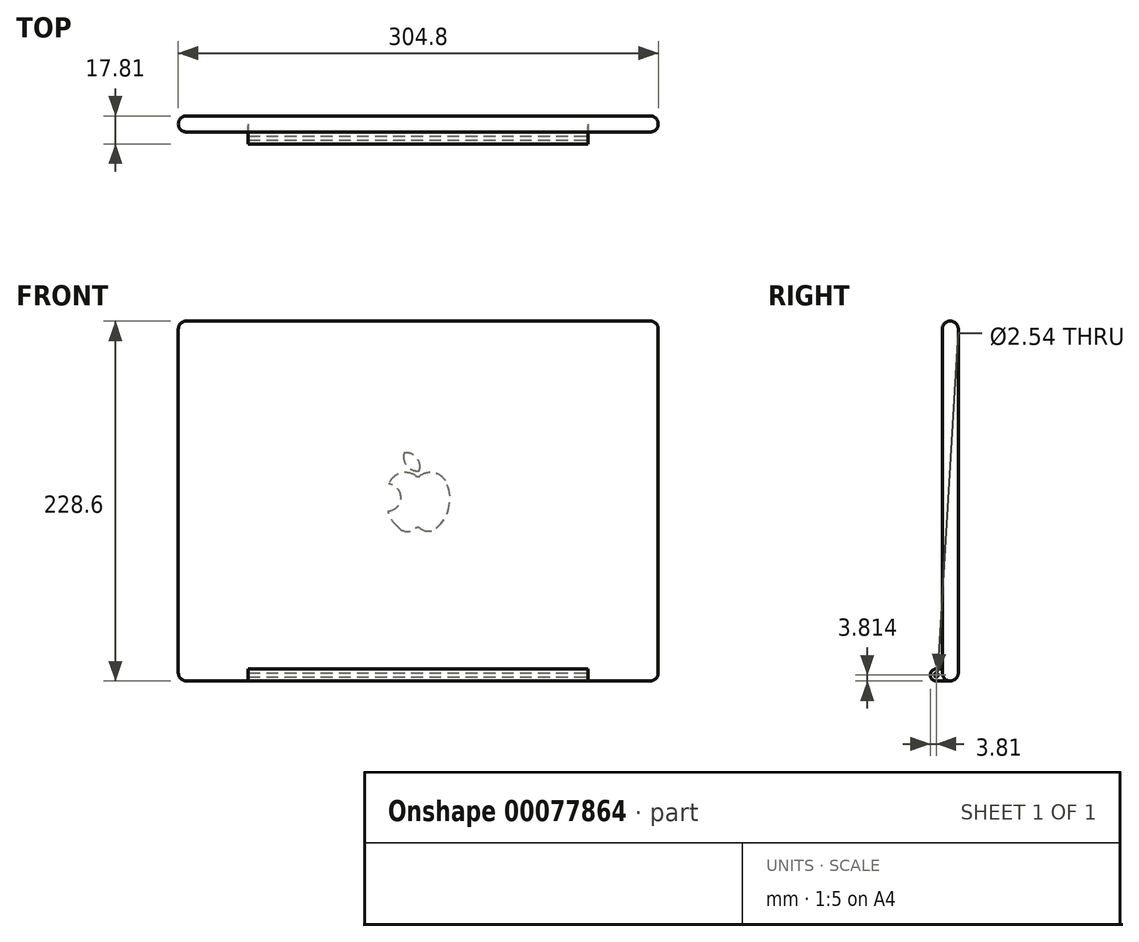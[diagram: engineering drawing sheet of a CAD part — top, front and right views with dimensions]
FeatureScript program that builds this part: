
annotation { "Feature Type Name" : "Feature", "Feature Type Description" : "" }
export const myFeature = defineFeature(function(context is Context, id is Id, definition is map)
    precondition{}
    {
        {
            var Q0;
            Q0=qCreatedBy(makeId("Front.planeOp"),FACE);
            var sketch = newSketch(context, id + "F0", { "sketchPlane" : qUnion([Q0])});
            skLineSegment(sketch, "E0.bottom", {"start": v(-207.35, 122.82) * mm, "end": v(97.45, 122.82) * mm});
            skLineSegment(sketch, "E0.top", {"start": v(-207.35, -105.78) * mm, "end": v(97.45, -105.78) * mm});
            skLineSegment(sketch, "E0.left", {"start": v(-207.35, 122.82) * mm, "end": v(-207.35, -105.78) * mm});
            skLineSegment(sketch, "E0.right", {"start": v(97.45, 122.82) * mm, "end": v(97.45, -105.78) * mm});
            skCircle(sketch, "E1", {"center": v(-54.95, 112.66) * mm, "radius": 3.18 * mm});
            skSolve(sketch);
        }
        {
            var Q0;
            Q0=makeQuery(id+"F0.imprint","IMPRINT",FACE,{"disambiguationData":[TD([[makeQuery(id+"F0.imprint","IMPRINT",EDGE,{"derivedFrom":sQuery(id+"F0.wireOp",EDGE,"E0.bottom")}),-1.0]])]});
            var Q1;
            Q1=makeQuery(id+"F0.imprint","IMPRINT",FACE,{"disambiguationData":[TD([[makeQuery(id+"F0.imprint","IMPRINT",EDGE,{"derivedFrom":sQuery(id+"F0.wireOp",EDGE,"E1")}),1.0]])]});
            extrude(context, id + "F1", {"entities" : qUnion([Q0, Q1]), "depth" : 7.62 * mm});
        }
        {
            var Q0;
            Q0=makeQuery(id+"F1.opExtrude","CAP_EDGE",EDGE,{"disambiguationData":[OSD([sQuery(id+"F0.wireOp",EDGE,"E0.bottom")])],"isStart":true});
            var Q1;
            Q1=makeQuery(id+"F1.opExtrude","CAP_EDGE",EDGE,{"disambiguationData":[OSD([sQuery(id+"F0.wireOp",EDGE,"E0.left")])],"isStart":true});
            var Q2;
            Q2=makeQuery(id+"F1.opExtrude","CAP_EDGE",EDGE,{"disambiguationData":[OSD([sQuery(id+"F0.wireOp",EDGE,"E0.right")])],"isStart":true});
            var Q3;
            Q3=makeQuery(id+"F1.opExtrude","CAP_EDGE",EDGE,{"disambiguationData":[OSD([sQuery(id+"F0.wireOp",EDGE,"E0.top")])],"isStart":true});
            var Q4;
            Q4=makeQuery(id+"F1.opExtrude","SWEPT_EDGE",EDGE,{"disambiguationData":[OSD([sQuery(id+"F0.wireOp",EDGE,"E0.bottom"),sQuery(id+"F0.wireOp",EDGE,"E0.right")])]});
            var Q5;
            Q5=makeQuery(id+"F1.opExtrude","SWEPT_EDGE",EDGE,{"disambiguationData":[OSD([sQuery(id+"F0.wireOp",EDGE,"E0.top"),sQuery(id+"F0.wireOp",EDGE,"E0.right")])]});
            var Q6;
            Q6=makeQuery(id+"F1.opExtrude","SWEPT_EDGE",EDGE,{"disambiguationData":[OSD([sQuery(id+"F0.wireOp",EDGE,"E0.bottom"),sQuery(id+"F0.wireOp",EDGE,"E0.left")])]});
            var Q7;
            Q7=makeQuery(id+"F1.opExtrude","SWEPT_EDGE",EDGE,{"disambiguationData":[OSD([sQuery(id+"F0.wireOp",EDGE,"E0.top"),sQuery(id+"F0.wireOp",EDGE,"E0.left")])]});
            fillet(context, id + "F2", {"entities" : qUnion([Q0, Q1, Q2, Q3, Q4, Q5, Q6, Q7]), "radius" : 5.08 * mm, "tangentPropagation" : true, "allowEdgeOverflow" : false});
        }
        {
            var Q0;
            Q0=makeQuery(id+"F1.opExtrude","CAP_FACE",FACE,{"disambiguationData":[OSD([sQuery(id+"F0.wireOp",EDGE,"E0.bottom"),sQuery(id+"F0.wireOp",EDGE,"E0.top"),sQuery(id+"F0.wireOp",EDGE,"E0.left"),sQuery(id+"F0.wireOp",EDGE,"E0.right")])],"isStart":false});
            var sketch = newSketch(context, id + "F3", { "sketchPlane" : qUnion([Q0])});
            skLineSegment(sketch, "E2.bottom", {"start": v(-188.3, 103.77) * mm, "end": v(78.4, 103.77) * mm});
            skLineSegment(sketch, "E2.top", {"start": v(-188.3, -80.38) * mm, "end": v(78.4, -80.38) * mm});
            skLineSegment(sketch, "E2.left", {"start": v(-188.3, 103.77) * mm, "end": v(-188.3, -80.38) * mm});
            skLineSegment(sketch, "E2.right", {"start": v(78.4, 103.77) * mm, "end": v(78.4, -80.38) * mm});
            skSolve(sketch);
        }
        {
            var Q0;
            Q0=makeQuery(id+"F3.imprint","IMPRINT",FACE,{"disambiguationData":[TD([[makeQuery(id+"F3.imprint","IMPRINT",EDGE,{"derivedFrom":sQuery(id+"F3.wireOp",EDGE,"E2.bottom")}),-1.0]])]});
            extrude(context, id + "F4", {"entities" : qUnion([Q0]), "operationType" : NewBodyOperationType.ADD, "depth" : 2.54 * mm});
        }
        {
            var Q0;
            Q0=makeQuery(id+"F3.imprint","IMPRINT",FACE,{"disambiguationData":[TD([[makeQuery(id+"F3.imprint","IMPRINT",EDGE,{"derivedFrom":sQuery(id+"F3.wireOp",EDGE,"E2.bottom")}),1.0]])]});
            extrude(context, id + "F5", {"entities" : qUnion([Q0]), "depth" : 2.54 * mm});
        }
        {
            var Q0;
            Q0=makeQuery(id+"F5.opExtrude","CAP_FACE",FACE,{"disambiguationData":[OSD([sQuery(id+"F0.wireOp",EDGE,"E0.bottom"),sQuery(id+"F0.wireOp",EDGE,"E0.top"),sQuery(id+"F0.wireOp",EDGE,"E0.left"),sQuery(id+"F0.wireOp",EDGE,"E0.right"),sQuery(id+"F3.wireOp",EDGE,"E2.bottom"),sQuery(id+"F3.wireOp",EDGE,"E2.top"),sQuery(id+"F3.wireOp",EDGE,"E2.left"),sQuery(id+"F3.wireOp",EDGE,"E2.right")])],"isStart":false});
            var sketch = newSketch(context, id + "F6", { "sketchPlane" : qUnion([Q0])});
            skLineSegment(sketch, "E3.bottom", {"start": v(-162.9, -105.78) * mm, "end": v(53, -105.78) * mm});
            skLineSegment(sketch, "E3.top", {"start": v(-162.9, -98.16) * mm, "end": v(53, -98.16) * mm});
            skLineSegment(sketch, "E3.left", {"start": v(-162.9, -105.78) * mm, "end": v(-162.9, -98.16) * mm});
            skLineSegment(sketch, "E3.right", {"start": v(53, -105.78) * mm, "end": v(53, -98.16) * mm});
            skSolve(sketch);
        }
        {
            var Q0;
            Q0=makeQuery(id+"F6.imprint","IMPRINT",FACE,{"disambiguationData":[TD([[makeQuery(id+"F6.imprint","IMPRINT",EDGE,{"derivedFrom":sQuery(id+"F6.wireOp",EDGE,"E3.bottom")}),1.0]])]});
            extrude(context, id + "F7", {"entities" : qUnion([Q0]), "operationType" : NewBodyOperationType.ADD, "depth" : 7.62 * mm});
        }
        {
            var Q0;
            Q0=makeQuery(id+"F7.opExtrude","SWEPT_FACE",FACE,{"disambiguationData":[OSD([sQuery(id+"F6.wireOp",EDGE,"E3.right")])]});
            var sketch = newSketch(context, id + "F8", { "sketchPlane" : qUnion([Q0])});
            skCircle(sketch, "E4", {"center": v(-13.97, -101.97) * mm, "radius": 1.27 * mm});
            skSolve(sketch);
        }
        {
            var Q0;
            Q0=makeQuery(id+"F7.opExtrude","CAP_EDGE",EDGE,{"disambiguationData":[OSD([sQuery(id+"F6.wireOp",EDGE,"E3.top")])],"isStart":false});
            var Q1;
            Q1=makeQuery(id+"F7.opExtrude","CAP_EDGE",EDGE,{"disambiguationData":[OSD([sQuery(id+"F6.wireOp",EDGE,"E3.bottom")])],"isStart":false});
            fillet(context, id + "F9", {"entities" : qUnion([Q0, Q1]), "radius" : 3.8 * mm, "tangentPropagation" : true, "allowEdgeOverflow" : false});
        }
        {
            var Q0;
            Q0=makeQuery(id+"F8.imprint","IMPRINT",FACE,{"disambiguationData":[TD([[makeQuery(id+"F8.imprint","IMPRINT",EDGE,{"derivedFrom":sQuery(id+"F8.wireOp",EDGE,"E4")}),1.0]])]});
            extrude(context, id + "F10", {"entities" : qUnion([Q0]), "operationType" : NewBodyOperationType.REMOVE, "oppositeDirection" : true, "depth" : 215.9 * mm});
        }
        {
            var Q0;
            Q0=makeQuery(id+"F0.imprint","IMPRINT",FACE,{"disambiguationData":[TD([[makeQuery(id+"F0.imprint","IMPRINT",EDGE,{"derivedFrom":sQuery(id+"F0.wireOp",EDGE,"E1")}),1.0]])]});
            extrude(context, id + "F11", {"entities" : qUnion([Q0]), "operationType" : NewBodyOperationType.ADD, "depth" : 10.16 * mm});
        }
        {
            var Q0;
            Q0=makeQuery(id+"F5.opExtrude","CAP_EDGE",EDGE,{"disambiguationData":[OSD([sQuery(id+"F0.wireOp",EDGE,"E0.left")])],"isStart":false});
            var Q1;
            {var subQ0=sQuery(id+"F0.wireOp",EDGE,"E0.bottom");var subQ1=sQuery(id+"F0.wireOp",EDGE,"E0.top");var subQ2=sQuery(id+"F0.wireOp",EDGE,"E0.left");var subQ3=sQuery(id+"F0.wireOp",EDGE,"E0.right");Q1=makeQuery(id+"F5.opExtrude","CAP_EDGE",EDGE,{"disambiguationData":[OSD([subQ0,subQ1,subQ2,subQ3]),TDD([makeQuery(id+"F3.imprint","IMPRINT",EDGE,{"derivedFrom":makeQuery(id+"F2.opFillet","BLEND_EDGE",EDGE,{"blendedFrom":[makeQuery(id+"F1.opExtrude","SWEPT_EDGE",EDGE,{"disambiguationData":[OSD([subQ0,subQ2])]}),makeQuery(id+"F1.opExtrude","CAP_FACE",FACE,{"disambiguationData":[OSD([subQ0,subQ1,subQ2,subQ3])],"isStart":false})],"blendedInto":[makeQuery(id+"F1.opExtrude","CAP_FACE",FACE,{"disambiguationData":[OSD([subQ0,subQ1,subQ2,subQ3])],"isStart":false})]})})])],"isStart":false});}
            var Q2;
            Q2=makeQuery(id+"F5.opExtrude","CAP_EDGE",EDGE,{"disambiguationData":[OSD([sQuery(id+"F0.wireOp",EDGE,"E0.bottom")])],"isStart":false});
            var Q3;
            {var subQ0=sQuery(id+"F0.wireOp",EDGE,"E0.bottom");var subQ1=sQuery(id+"F0.wireOp",EDGE,"E0.top");var subQ2=sQuery(id+"F0.wireOp",EDGE,"E0.left");var subQ3=sQuery(id+"F0.wireOp",EDGE,"E0.right");Q3=makeQuery(id+"F5.opExtrude","CAP_EDGE",EDGE,{"disambiguationData":[OSD([subQ0,subQ1,subQ2,subQ3]),TDD([makeQuery(id+"F3.imprint","IMPRINT",EDGE,{"derivedFrom":makeQuery(id+"F2.opFillet","BLEND_EDGE",EDGE,{"blendedFrom":[makeQuery(id+"F1.opExtrude","SWEPT_EDGE",EDGE,{"disambiguationData":[OSD([subQ0,subQ3])]}),makeQuery(id+"F1.opExtrude","CAP_FACE",FACE,{"disambiguationData":[OSD([subQ0,subQ1,subQ2,subQ3])],"isStart":false})],"blendedInto":[makeQuery(id+"F1.opExtrude","CAP_FACE",FACE,{"disambiguationData":[OSD([subQ0,subQ1,subQ2,subQ3])],"isStart":false})]})})])],"isStart":false});}
            var Q4;
            Q4=makeQuery(id+"F5.opExtrude","CAP_EDGE",EDGE,{"disambiguationData":[OSD([sQuery(id+"F0.wireOp",EDGE,"E0.right")])],"isStart":false});
            var Q5;
            {var subQ0=sQuery(id+"F0.wireOp",EDGE,"E0.top");Q5=makeQuery(id+"F7.boolean.opBoolean","SPLIT",EDGE,{"disambiguationData":[TD([makeQuery(id+"F7.opExtrude","SWEPT_FACE",FACE,{"disambiguationData":[OSD([sQuery(id+"F6.wireOp",EDGE,"E3.left")])]})])],"derivedFrom":makeQuery(id+"F5.opExtrude","CAP_EDGE",EDGE,{"disambiguationData":[OSD([subQ0])],"isStart":false})});}
            var Q6;
            {var subQ0=sQuery(id+"F0.wireOp",EDGE,"E0.bottom");var subQ1=sQuery(id+"F0.wireOp",EDGE,"E0.top");var subQ2=sQuery(id+"F0.wireOp",EDGE,"E0.left");var subQ3=sQuery(id+"F0.wireOp",EDGE,"E0.right");Q6=makeQuery(id+"F5.opExtrude","CAP_EDGE",EDGE,{"disambiguationData":[OSD([subQ0,subQ1,subQ2,subQ3]),TDD([makeQuery(id+"F3.imprint","IMPRINT",EDGE,{"derivedFrom":makeQuery(id+"F2.opFillet","BLEND_EDGE",EDGE,{"blendedFrom":[makeQuery(id+"F1.opExtrude","SWEPT_EDGE",EDGE,{"disambiguationData":[OSD([subQ1,subQ2])]}),makeQuery(id+"F1.opExtrude","CAP_FACE",FACE,{"disambiguationData":[OSD([subQ0,subQ1,subQ2,subQ3])],"isStart":false})],"blendedInto":[makeQuery(id+"F1.opExtrude","CAP_FACE",FACE,{"disambiguationData":[OSD([subQ0,subQ1,subQ2,subQ3])],"isStart":false})]})})])],"isStart":false});}
            var Q7;
            {var subQ0=sQuery(id+"F0.wireOp",EDGE,"E0.top");Q7=makeQuery(id+"F7.boolean.opBoolean","SPLIT",EDGE,{"disambiguationData":[TD([makeQuery(id+"F7.opExtrude","SWEPT_FACE",FACE,{"disambiguationData":[OSD([sQuery(id+"F6.wireOp",EDGE,"E3.right")])]})])],"derivedFrom":makeQuery(id+"F5.opExtrude","CAP_EDGE",EDGE,{"disambiguationData":[OSD([subQ0])],"isStart":false})});}
            var Q8;
            {var subQ0=sQuery(id+"F0.wireOp",EDGE,"E0.bottom");var subQ1=sQuery(id+"F0.wireOp",EDGE,"E0.top");var subQ2=sQuery(id+"F0.wireOp",EDGE,"E0.left");var subQ3=sQuery(id+"F0.wireOp",EDGE,"E0.right");Q8=makeQuery(id+"F5.opExtrude","CAP_EDGE",EDGE,{"disambiguationData":[OSD([subQ0,subQ1,subQ2,subQ3]),TDD([makeQuery(id+"F3.imprint","IMPRINT",EDGE,{"derivedFrom":makeQuery(id+"F2.opFillet","BLEND_EDGE",EDGE,{"blendedFrom":[makeQuery(id+"F1.opExtrude","SWEPT_EDGE",EDGE,{"disambiguationData":[OSD([subQ1,subQ3])]}),makeQuery(id+"F1.opExtrude","CAP_FACE",FACE,{"disambiguationData":[OSD([subQ0,subQ1,subQ2,subQ3])],"isStart":false})],"blendedInto":[makeQuery(id+"F1.opExtrude","CAP_FACE",FACE,{"disambiguationData":[OSD([subQ0,subQ1,subQ2,subQ3])],"isStart":false})]})})])],"isStart":false});}
            fillet(context, id + "F12", {"entities" : qUnion([Q0, Q1, Q2, Q3, Q4, Q5, Q6, Q7, Q8]), "radius" : 5 * mm, "tangentPropagation" : true, "allowEdgeOverflow" : false});
        }
        {
            var Q0;
            Q0=makeQuery(id+"F1.opExtrude","CAP_FACE",FACE,{"disambiguationData":[OSD([sQuery(id+"F0.wireOp",EDGE,"E0.bottom"),sQuery(id+"F0.wireOp",EDGE,"E0.top"),sQuery(id+"F0.wireOp",EDGE,"E0.left"),sQuery(id+"F0.wireOp",EDGE,"E0.right")])],"isStart":true});
            var sketch = newSketch(context, id + "F13", { "sketchPlane" : qUnion([Q0])});
            skArc(sketch, "E5", {"start": v(37.75, 21.54) * mm, "mid": v(35.3, 5.32) * mm, "end": v(43.55, -8.86) * mm});
            skArc(sketch, "E6", {"start": v(43.55, -8.86) * mm, "mid": v(48.63, -10.62) * mm, "end": v(53.71, -8.86) * mm});
            skArc(sketch, "E7", {"start": v(56.84, -8.86) * mm, "mid": v(55.28, -8.33) * mm, "end": v(53.71, -8.86) * mm});
            skArc(sketch, "E8", {"start": v(56.84, -8.86) * mm, "mid": v(61.92, -10.83) * mm, "end": v(67, -8.86) * mm});
            skFitSpline(sketch, "E9", {"points": [v(67, -8.86) * mm, v(70.5, -5.22) * mm, v(72.86, -1.79) * mm, v(73.93, 1.88) * mm, v(73.69, 2.24) * mm], "startDerivative": vector(11.37, 11.44) * mm, "endDerivative": vector(-3.24, 2.43) * mm});
            skArc(sketch, "E10", {"start": v(73.8, 19.3) * mm, "mid": v(65.96, 10.73) * mm, "end": v(73.8, 2.16) * mm});
            skArc(sketch, "E11", {"start": v(73.8, 19.3) * mm, "mid": v(66.5, 26.06) * mm, "end": v(56.68, 24.62) * mm});
            skArc(sketch, "E12", {"start": v(53.76, 24.62) * mm, "mid": v(45.11, 26.43) * mm, "end": v(37.75, 21.54) * mm});
            skArc(sketch, "E13", {"start": v(53.76, 24.62) * mm, "mid": v(55.22, 24) * mm, "end": v(56.68, 24.62) * mm});
            skArc(sketch, "E14", {"start": v(63.95, 38.98) * mm, "mid": v(55.91, 36.05) * mm, "end": v(54.38, 27.64) * mm});
            skArc(sketch, "E15", {"start": v(54.38, 27.64) * mm, "mid": v(62.17, 30.77) * mm, "end": v(63.95, 38.98) * mm});
            skLineSegment(sketch, "E16", {"start": v(-92.37, 117.74) * mm, "end": v(202.27, -100.7) * mm, "construction": true});
            skLineSegment(sketch, "E17", {"start": v(202.27, -100.7) * mm, "end": v(202.27, 117.74) * mm, "construction": true});
            skLineSegment(sketch, "E18", {"start": v(202.27, 117.74) * mm, "end": v(-92.37, -100.7) * mm, "construction": true});
            skSolve(sketch);
        }
        {
            var Q0;
            Q0=makeQuery(id+"F13.imprint","IMPRINT",FACE,{"disambiguationData":[TD([[makeQuery(id+"F13.imprint","IMPRINT",EDGE,{"derivedFrom":sQuery(id+"F13.wireOp",EDGE,"E5")}),1.0]])]});
            var Q1;
            Q1=makeQuery(id+"F13.imprint","IMPRINT",FACE,{"disambiguationData":[TD([[makeQuery(id+"F13.imprint","IMPRINT",EDGE,{"derivedFrom":sQuery(id+"F13.wireOp",EDGE,"E14")}),1.0]])]});
            extrude(context, id + "F14", {"entities" : qUnion([Q0, Q1]), "depth" : 0.03 * mm});
        }
    });
